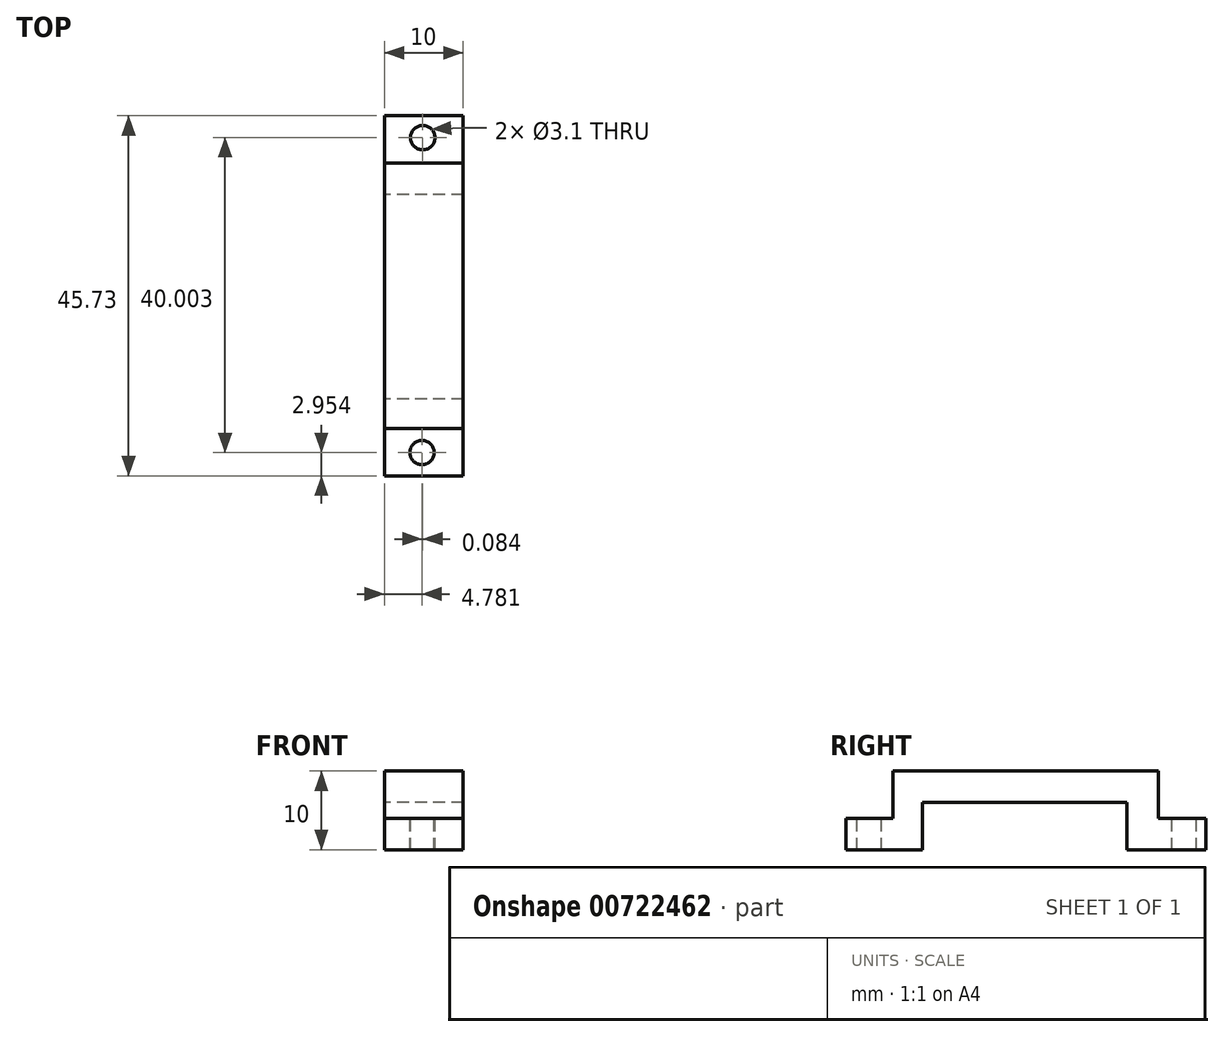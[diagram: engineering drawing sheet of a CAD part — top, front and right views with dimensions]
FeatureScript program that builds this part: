
annotation { "Feature Type Name" : "Feature", "Feature Type Description" : "" }
export const myFeature = defineFeature(function(context is Context, id is Id, definition is map)
    precondition{}
    {
        {
            var Q0;
            Q0=qCreatedBy(makeId("Right.planeOp"),FACE);
            var sketch = newSketch(context, id + "F0", { "sketchPlane" : qUnion([Q0])});
            skLineSegment(sketch, "E0.bottom", {"start": v(-8.1, 0) * mm, "end": v(17.9, 0) * mm});
            skLineSegment(sketch, "E0.top", {"start": v(-8.1, -4) * mm, "end": v(17.9, -4) * mm});
            skLineSegment(sketch, "E0.left", {"start": v(-8.1, 0) * mm, "end": v(-8.1, -4) * mm});
            skLineSegment(sketch, "E0.right", {"start": v(17.9, 0) * mm, "end": v(17.9, -4) * mm});
            skLineSegment(sketch, "E1.bottom", {"start": v(-8.1, 0) * mm, "end": v(-11.83, 0) * mm});
            skLineSegment(sketch, "E1.top", {"start": v(-8.1, -10) * mm, "end": v(-11.83, -10) * mm});
            skLineSegment(sketch, "E1.left", {"start": v(-8.1, 0) * mm, "end": v(-8.1, -10) * mm});
            skLineSegment(sketch, "E1.right", {"start": v(-11.83, 0) * mm, "end": v(-11.83, -10) * mm});
            skLineSegment(sketch, "E2.bottom", {"start": v(-11.83, -10) * mm, "end": v(-17.83, -10) * mm});
            skLineSegment(sketch, "E2.top", {"start": v(-11.83, -6) * mm, "end": v(-17.83, -6) * mm});
            skLineSegment(sketch, "E2.left", {"start": v(-11.83, -10) * mm, "end": v(-11.83, -6) * mm});
            skLineSegment(sketch, "E2.right", {"start": v(-17.83, -10) * mm, "end": v(-17.83, -6) * mm});
            skLineSegment(sketch, "E3.bottom", {"start": v(17.9, 0) * mm, "end": v(21.9, 0) * mm});
            skLineSegment(sketch, "E3.top", {"start": v(17.9, -10) * mm, "end": v(21.9, -10) * mm});
            skLineSegment(sketch, "E3.left", {"start": v(17.9, 0) * mm, "end": v(17.9, -10) * mm});
            skLineSegment(sketch, "E3.right", {"start": v(21.9, 0) * mm, "end": v(21.9, -10) * mm});
            skLineSegment(sketch, "E4.bottom", {"start": v(21.9, -10) * mm, "end": v(27.9, -10) * mm});
            skLineSegment(sketch, "E4.top", {"start": v(21.9, -6) * mm, "end": v(27.9, -6) * mm});
            skLineSegment(sketch, "E4.left", {"start": v(21.9, -10) * mm, "end": v(21.9, -6) * mm});
            skLineSegment(sketch, "E4.right", {"start": v(27.9, -10) * mm, "end": v(27.9, -6) * mm});
            skSolve(sketch);
        }
        {
            var Q0;
            {var subQ3=sQuery(id+"F0.wireOp",EDGE,"E1.bottom");Q0=makeQuery(id+"F0.imprint","IMPRINT",FACE,{"disambiguationData":[TD([[makeQuery(id+"F0.imprint","IMPRINT",EDGE,{"derivedFrom":subQ3}),1.0]])]});}
            var Q1;
            Q1=makeQuery(id+"F0.imprint","IMPRINT",FACE,{"disambiguationData":[TD([[makeQuery(id+"F0.imprint","IMPRINT",EDGE,{"derivedFrom":sQuery(id+"F0.wireOp",EDGE,"E2.bottom")}),-1.0]])]});
            var Q2;
            {var subQ0=sQuery(id+"F0.wireOp",EDGE,"E0.bottom");Q2=makeQuery(id+"F0.imprint","IMPRINT",FACE,{"disambiguationData":[TD([[makeQuery(id+"F0.imprint","IMPRINT",EDGE,{"derivedFrom":subQ0}),-1.0]])]});}
            var Q3;
            {var subQ3=sQuery(id+"F0.wireOp",EDGE,"E3.bottom");Q3=makeQuery(id+"F0.imprint","IMPRINT",FACE,{"disambiguationData":[TD([[makeQuery(id+"F0.imprint","IMPRINT",EDGE,{"derivedFrom":subQ3}),-1.0]])]});}
            var Q4;
            Q4=makeQuery(id+"F0.imprint","IMPRINT",FACE,{"disambiguationData":[TD([[makeQuery(id+"F0.imprint","IMPRINT",EDGE,{"derivedFrom":sQuery(id+"F0.wireOp",EDGE,"E4.bottom")}),1.0]])]});
            extrude(context, id + "F1", {"entities" : qUnion([Q0, Q1, Q2, Q3, Q4]), "depth" : 10 * mm, "offsetDistance" : 25 * mm});
        }
        {
            var Q0;
            Q0=qCreatedBy(makeId("Top.planeOp"),FACE);
            var sketch = newSketch(context, id + "F2", { "sketchPlane" : qUnion([Q0])});
            skCircle(sketch, "E5", {"center": v(4.78, -14.88) * mm, "radius": 1.55 * mm});
            skCircle(sketch, "E6", {"center": v(4.87, 25.13) * mm, "radius": 1.55 * mm});
            skSolve(sketch);
        }
        {
            var Q0;
            Q0=sQuery(id+"F2.wireOp",VERTEX,"E5.center");
            var Q1;
            Q1=sQuery(id+"F2.wireOp",VERTEX,"E6.center");
            var Q2;
            Q2=makeQuery(id+"F1.opExtrude","SWEPT_BODY",BODY,{"disambiguationData":[OSD([sQuery(id+"F0.wireOp",EDGE,"E0.bottom"),sQuery(id+"F0.wireOp",EDGE,"E0.top"),sQuery(id+"F0.wireOp",EDGE,"E1.bottom"),sQuery(id+"F0.wireOp",EDGE,"E1.top"),sQuery(id+"F0.wireOp",EDGE,"E1.left"),sQuery(id+"F0.wireOp",EDGE,"E1.right"),sQuery(id+"F0.wireOp",EDGE,"E2.bottom"),sQuery(id+"F0.wireOp",EDGE,"E2.top"),sQuery(id+"F0.wireOp",EDGE,"E2.right"),sQuery(id+"F0.wireOp",EDGE,"E3.bottom"),sQuery(id+"F0.wireOp",EDGE,"E3.top"),sQuery(id+"F0.wireOp",EDGE,"E3.left"),sQuery(id+"F0.wireOp",EDGE,"E3.right"),sQuery(id+"F0.wireOp",EDGE,"E4.bottom"),sQuery(id+"F0.wireOp",EDGE,"E4.top"),sQuery(id+"F0.wireOp",EDGE,"E4.right")])]});
            hole(context, id + "F3", {"style" : HoleStyle.SIMPLE, "endStyle" : HoleEndStyle.THROUGH, "holeDiameter" : 3.1 * mm, "majorDiameter" : 5 * mm, "isTappedThrough" : true, "tappedDepth" : 12 * mm, "tapClearance" : 3, "locations" : qUnion([Q0, Q1]), "scope" : qUnion([Q2])});
        }
    });
